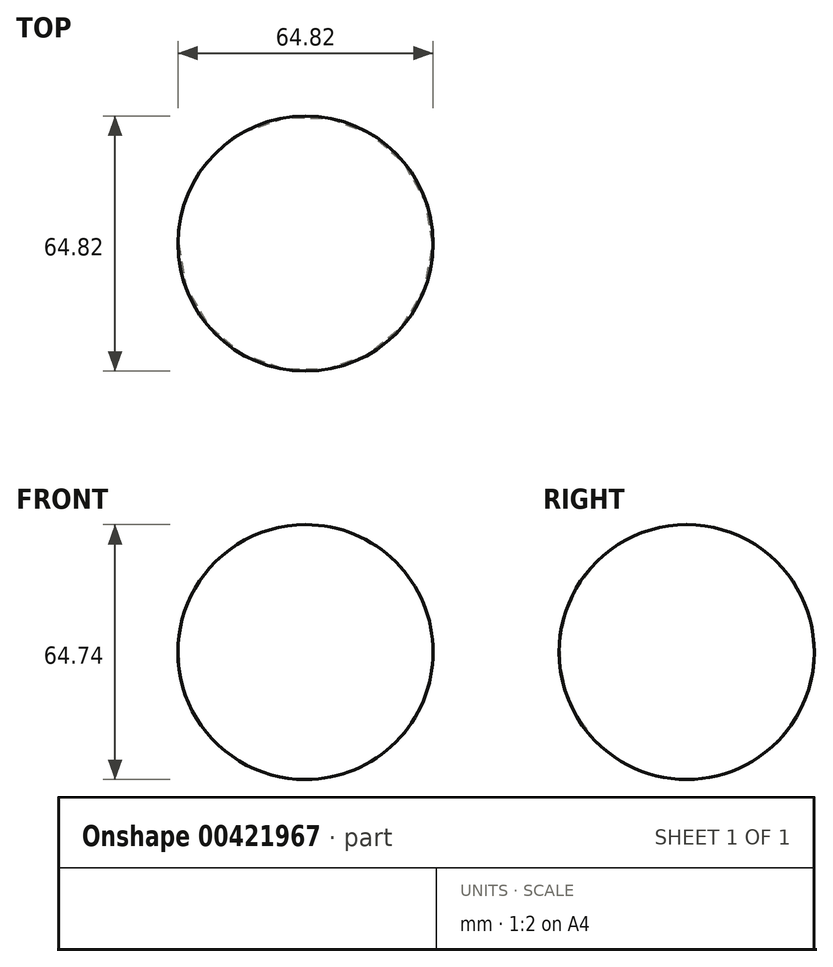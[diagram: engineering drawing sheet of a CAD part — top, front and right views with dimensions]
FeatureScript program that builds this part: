
annotation { "Feature Type Name" : "Feature", "Feature Type Description" : "" }
export const myFeature = defineFeature(function(context is Context, id is Id, definition is map)
    precondition{}
    {
        {
            var Q0;
            Q0=qCreatedBy(makeId("Front.planeOp"),FACE);
            var sketch = newSketch(context, id + "F0", { "sketchPlane" : qUnion([Q0])});
            skLineSegment(sketch, "E0", {"start": v(0, 31.32) * mm, "end": v(0, -33.42) * mm});
            skArc(sketch, "E1", {"start": v(0, -33.42) * mm, "mid": v(32.41, -1.05) * mm, "end": v(0, 31.32) * mm});
            skSolve(sketch);
        }
        {
            var Q0;
            Q0=makeQuery(id+"F0.imprint","IMPRINT",FACE,{"disambiguationData":[TD([[makeQuery(id+"F0.imprint","IMPRINT",EDGE,{"derivedFrom":sQuery(id+"F0.wireOp",EDGE,"E0")}),1.0]])]});
            var Q1;
            Q1=sQuery(id+"F0.wireOp",EDGE,"E0");
            revolve(context, id + "F1", {"entities" : qUnion([Q0]), "axis" : qUnion([Q1]), "revolveType" : RevolveType.FULL});
        }
    });
